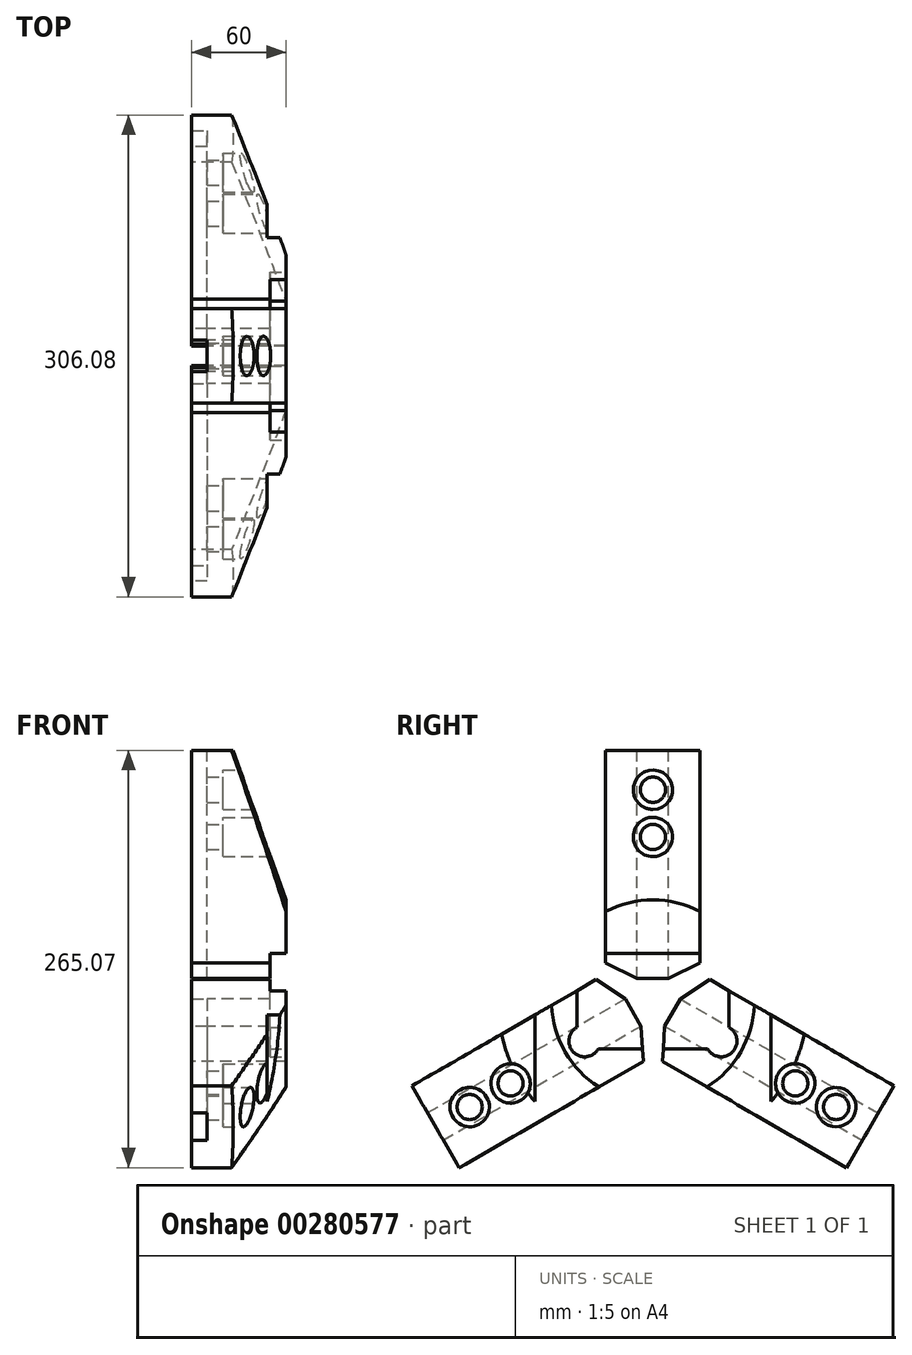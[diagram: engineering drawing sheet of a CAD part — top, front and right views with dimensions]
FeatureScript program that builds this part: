
annotation { "Feature Type Name" : "Feature", "Feature Type Description" : "" }
export const myFeature = defineFeature(function(context is Context, id is Id, definition is map)
    precondition{}
    {
        {
            var Q0;
            Q0=qCreatedBy(makeId("Right.planeOp"),FACE);
            var sketch = newSketch(context, id + "F0", { "sketchPlane" : qUnion([Q0])});
            skCircle(sketch, "E0", {"center": v(0, 0) * mm, "radius": 14.4 * mm});
            skLineSegment(sketch, "E1", {"start": v(0, 198.34) * mm, "end": v(0, 14.4) * mm, "construction": true});
            skLineSegment(sketch, "E2", {"start": v(0, 14.39) * mm, "end": v(0, -30.8) * mm, "construction": true});
            skLineSegment(sketch, "E3", {"start": v(0, 14.39) * mm, "end": v(10, 14.4) * mm});
            skLineSegment(sketch, "E4", {"start": v(10, 14.4) * mm, "end": v(30, 24.39) * mm});
            skLineSegment(sketch, "E5", {"start": v(30, 24.39) * mm, "end": v(30, 159.39) * mm});
            skLineSegment(sketch, "E6", {"start": v(30, 159.39) * mm, "end": v(0, 159.39) * mm});
            skLineSegment(sketch, "E7", {"start": v(0, 159.39) * mm, "end": v(-30, 159.39) * mm});
            skLineSegment(sketch, "E8", {"start": v(-30, 159.39) * mm, "end": v(-30, 24.39) * mm});
            skLineSegment(sketch, "E9", {"start": v(-30, 24.39) * mm, "end": v(-10, 14.39) * mm});
            skLineSegment(sketch, "E10", {"start": v(-10, 14.4) * mm, "end": v(0, 14.4) * mm});
            skSolve(sketch);
        }
        {
            var Q0;
            Q0=makeQuery(id+"F0.imprint","IMPRINT",FACE,{"disambiguationData":[TD([[makeQuery(id+"F0.imprint","IMPRINT",EDGE,{"derivedFrom":sQuery(id+"F0.wireOp",EDGE,"E3")}),1.0]])]});
            extrude(context, id + "F1", {"entities" : qUnion([Q0]), "depth" : 60 * mm});
        }
        {
            var Q0;
            Q0=makeQuery(id+"F1.opExtrude","CAP_FACE",FACE,{"disambiguationData":[OSD([sQuery(id+"F0.wireOp",EDGE,"E3"),sQuery(id+"F0.wireOp",EDGE,"E4"),sQuery(id+"F0.wireOp",EDGE,"E5"),sQuery(id+"F0.wireOp",EDGE,"E6"),sQuery(id+"F0.wireOp",EDGE,"E7"),sQuery(id+"F0.wireOp",EDGE,"E8"),sQuery(id+"F0.wireOp",EDGE,"E9"),sQuery(id+"F0.wireOp",EDGE,"E10")])],"isStart":false});
            var sketch = newSketch(context, id + "F2", { "sketchPlane" : qUnion([Q0])});
            skCircle(sketch, "E11", {"center": v(0, 134.39) * mm, "radius": 8 * mm});
            skCircle(sketch, "E12", {"center": v(0, 104.39) * mm, "radius": 8 * mm});
            skCircle(sketch, "E13", {"center": v(0, 134.39) * mm, "radius": 12.5 * mm});
            skCircle(sketch, "E14", {"center": v(0, 104.39) * mm, "radius": 12.5 * mm});
            skSolve(sketch);
        }
        {
            var Q0;
            Q0=makeQuery(id+"F2.imprint","IMPRINT",FACE,{"disambiguationData":[TD([[makeQuery(id+"F2.imprint","IMPRINT",EDGE,{"derivedFrom":sQuery(id+"F2.wireOp",EDGE,"E11")}),1.0]])]});
            var Q1;
            Q1=makeQuery(id+"F2.imprint","IMPRINT",FACE,{"disambiguationData":[TD([[makeQuery(id+"F2.imprint","IMPRINT",EDGE,{"derivedFrom":sQuery(id+"F2.wireOp",EDGE,"E12")}),1.0]])]});
            extrude(context, id + "F3", {"entities" : qUnion([Q0, Q1]), "operationType" : NewBodyOperationType.REMOVE, "endBound" : BoundingType.UP_TO_NEXT, "oppositeDirection" : true, "depth" : 25 * mm});
        }
        {
            var Q0;
            Q0=qSketchRegion(id+"F2",true);
            extrude(context, id + "F4", {"entities" : qUnion([Q0]), "operationType" : NewBodyOperationType.REMOVE, "oppositeDirection" : true, "depth" : 40 * mm});
        }
        {
            var Q0;
            Q0=makeQuery(id+"F1.opExtrude","SWEPT_FACE",FACE,{"disambiguationData":[OSD([sQuery(id+"F0.wireOp",EDGE,"E6"),sQuery(id+"F0.wireOp",EDGE,"E7")])]});
            var sketch = newSketch(context, id + "F5", { "sketchPlane" : qUnion([Q0])});
            skLineSegment(sketch, "E15", {"start": v(0, 0) * mm, "end": v(0, -10) * mm});
            skLineSegment(sketch, "E16", {"start": v(0, -10) * mm, "end": v(10, -10) * mm});
            skLineSegment(sketch, "E17", {"start": v(10, -10) * mm, "end": v(10, 0) * mm});
            skLineSegment(sketch, "E18", {"start": v(10, 0) * mm, "end": v(10, 10) * mm});
            skLineSegment(sketch, "E19", {"start": v(10, 10) * mm, "end": v(0, 10) * mm});
            skLineSegment(sketch, "E20", {"start": v(0, 10) * mm, "end": v(0, 0) * mm});
            skSolve(sketch);
        }
        {
            var Q0;
            Q0=qSketchRegion(id+"F5",true);
            var Q1;
            Q1=makeQuery(id+"F1.opExtrude","SWEPT_FACE",FACE,{"disambiguationData":[OSD([sQuery(id+"F0.wireOp",EDGE,"E3"),sQuery(id+"F0.wireOp",EDGE,"E10")])]});
            extrude(context, id + "F6", {"entities" : qUnion([Q0]), "operationType" : NewBodyOperationType.REMOVE, "endBound" : BoundingType.UP_TO_SURFACE, "oppositeDirection" : true, "endBoundEntityFace" : qUnion([Q1]), "depth" : 25 * mm});
        }
        {
            var Q0;
            Q0=qCreatedBy(makeId("Front.planeOp"),FACE);
            var sketch = newSketch(context, id + "F7", { "sketchPlane" : qUnion([Q0])});
            skLineSegment(sketch, "E21", {"start": v(0, 0) * mm, "end": v(73.98, 0) * mm, "construction": true});
            skSolve(sketch);
        }
        {
            var Q0;
            Q0=makeQuery(id+"F1.opExtrude","SWEPT_BODY",BODY,{"disambiguationData":[OSD([sQuery(id+"F0.wireOp",EDGE,"E3"),sQuery(id+"F0.wireOp",EDGE,"E4"),sQuery(id+"F0.wireOp",EDGE,"E5"),sQuery(id+"F0.wireOp",EDGE,"E6"),sQuery(id+"F0.wireOp",EDGE,"E7"),sQuery(id+"F0.wireOp",EDGE,"E8"),sQuery(id+"F0.wireOp",EDGE,"E9"),sQuery(id+"F0.wireOp",EDGE,"E10")])]});
            var Q1;
            Q1=sQuery(id+"F7.wireOp",EDGE,"E21");
            circularPattern(context, id + "F8", {"entities" : qUnion([Q0]), "axis" : qUnion([Q1]), "angle" : 360 * degree, "instanceCount" : 3, "equalSpace" : true, "computeTransformsWithoutBuiltin" : true});
        }
        {
            var Q0;
            Q0=makeQuery(id+"F1.opExtrude","SWEPT_BODY",BODY,{"disambiguationData":[OSD([sQuery(id+"F0.wireOp",EDGE,"E3"),sQuery(id+"F0.wireOp",EDGE,"E4"),sQuery(id+"F0.wireOp",EDGE,"E5"),sQuery(id+"F0.wireOp",EDGE,"E6"),sQuery(id+"F0.wireOp",EDGE,"E7"),sQuery(id+"F0.wireOp",EDGE,"E8"),sQuery(id+"F0.wireOp",EDGE,"E9"),sQuery(id+"F0.wireOp",EDGE,"E10")])]});
            var Q1;
            Q1=makeQuery(id+"F8.opPattern","COPY",BODY,{"derivedFrom":makeQuery(id+"F1.opExtrude","SWEPT_BODY",BODY,{"disambiguationData":[OSD([sQuery(id+"F0.wireOp",EDGE,"E3"),sQuery(id+"F0.wireOp",EDGE,"E4"),sQuery(id+"F0.wireOp",EDGE,"E5"),sQuery(id+"F0.wireOp",EDGE,"E6"),sQuery(id+"F0.wireOp",EDGE,"E7"),sQuery(id+"F0.wireOp",EDGE,"E8"),sQuery(id+"F0.wireOp",EDGE,"E9"),sQuery(id+"F0.wireOp",EDGE,"E10")])]}),"instanceName":"1"});
            var Q2;
            Q2=makeQuery(id+"F8.opPattern","COPY",BODY,{"derivedFrom":makeQuery(id+"F1.opExtrude","SWEPT_BODY",BODY,{"disambiguationData":[OSD([sQuery(id+"F0.wireOp",EDGE,"E3"),sQuery(id+"F0.wireOp",EDGE,"E4"),sQuery(id+"F0.wireOp",EDGE,"E5"),sQuery(id+"F0.wireOp",EDGE,"E6"),sQuery(id+"F0.wireOp",EDGE,"E7"),sQuery(id+"F0.wireOp",EDGE,"E8"),sQuery(id+"F0.wireOp",EDGE,"E9"),sQuery(id+"F0.wireOp",EDGE,"E10")])]}),"instanceName":"2"});
            transform(context, id + "F9", {"entities" : qUnion([Q0, Q1, Q2]), "transformType" : TransformType.TRANSLATION_3D, "dx" : 3 * mm, "dy" : 0 * mm, "dz" : 0 * mm, "makeCopy" : false});
        }
        {
            var Q0;
            Q0=makeQuery(id+"F1.opExtrude","CAP_FACE",FACE,{"disambiguationData":[OSD([sQuery(id+"F0.wireOp",EDGE,"E3"),sQuery(id+"F0.wireOp",EDGE,"E4"),sQuery(id+"F0.wireOp",EDGE,"E5"),sQuery(id+"F0.wireOp",EDGE,"E6"),sQuery(id+"F0.wireOp",EDGE,"E7"),sQuery(id+"F0.wireOp",EDGE,"E8"),sQuery(id+"F0.wireOp",EDGE,"E9"),sQuery(id+"F0.wireOp",EDGE,"E10")])],"isStart":false});
            var sketch = newSketch(context, id + "F10", { "sketchPlane" : qUnion([Q0])});
            skLineSegment(sketch, "E22.bottom", {"start": v(-34.71, -30.25) * mm, "end": v(34.71, -30.25) * mm});
            skLineSegment(sketch, "E22.top", {"start": v(-34.71, 30.25) * mm, "end": v(34.71, 30.25) * mm});
            skLineSegment(sketch, "E22.left", {"start": v(-48.38, -16.59) * mm, "end": v(-48.38, 16.59) * mm});
            skLineSegment(sketch, "E22.right", {"start": v(48.38, -16.59) * mm, "end": v(48.38, 16.59) * mm});
            skPoint(sketch, "E22.middle", {"position": v(0, 0) * mm});
            skPoint(sketch, "E23", {"position": v(-43.38, 25.25) * mm});
            skPoint(sketch, "E24", {"position": v(43.38, 25.25) * mm});
            skPoint(sketch, "E25", {"position": v(-43.38, -25.25) * mm});
            skPoint(sketch, "E26", {"position": v(43.38, -25.25) * mm});
            skArc(sketch, "E27", {"start": v(-34.71, 30.25) * mm, "mid": v(-50.45, 32.32) * mm, "end": v(-48.38, 16.59) * mm});
            skArc(sketch, "E28", {"start": v(48.37, 16.59) * mm, "mid": v(50.45, 32.32) * mm, "end": v(34.71, 30.25) * mm});
            skArc(sketch, "E29", {"start": v(34.71, -30.25) * mm, "mid": v(50.45, -32.32) * mm, "end": v(48.38, -16.59) * mm});
            skArc(sketch, "E30", {"start": v(-48.38, -16.59) * mm, "mid": v(-50.45, -32.32) * mm, "end": v(-34.71, -30.25) * mm});
            skSolve(sketch);
        }
        {
            var Q0;
            Q0=makeQuery(id+"F10.imprint","IMPRINT",FACE,{"disambiguationData":[TD([[makeQuery(id+"F10.imprint","IMPRINT",EDGE,{"derivedFrom":sQuery(id+"F10.wireOp",EDGE,"E22.bottom")}),1.0]])]});
            var Q1;
            {var subQ5=makeQuery(id+"F1.opExtrude","CAP_EDGE",EDGE,{"disambiguationData":[OSD([sQuery(id+"F0.wireOp",EDGE,"E3"),sQuery(id+"F0.wireOp",EDGE,"E10")])],"isStart":false});Q1=makeQuery(id+"F10.imprint","IMPRINT",FACE,{"disambiguationData":[TD([[makeQuery(id+"F10.imprint","IMPRINT",EDGE,{"derivedFrom":subQ5}),1.0]])]});}
            extrude(context, id + "F11", {"entities" : qUnion([Q0, Q1]), "operationType" : NewBodyOperationType.REMOVE, "oppositeDirection" : true, "depth" : 10.3 * mm, "offsetDistance" : 25 * mm});
        }
        {
            var Q0;
            Q0=qCreatedBy(makeId("Front.planeOp"),FACE);
            var sketch = newSketch(context, id + "F12", { "sketchPlane" : qUnion([Q0])});
            skLineSegment(sketch, "E31", {"start": v(0, 0) * mm, "end": v(61.97, 0) * mm, "construction": true});
            skLineSegment(sketch, "E32", {"start": v(29.5, 159.39) * mm, "end": v(63, 64.39) * mm});
            skLineSegment(sketch, "E33", {"start": v(63, 64.39) * mm, "end": v(63, 159.39) * mm});
            skLineSegment(sketch, "E34", {"start": v(63, 159.39) * mm, "end": v(29.5, 159.39) * mm});
            skLineSegment(sketch, "E35", {"start": v(29.5, 159.39) * mm, "end": v(28.09, 163.39) * mm});
            skLineSegment(sketch, "E36", {"start": v(28.09, 163.39) * mm, "end": v(63, 163.39) * mm});
            skLineSegment(sketch, "E37", {"start": v(63, 163.39) * mm, "end": v(63, 159.39) * mm});
            skSolve(sketch);
        }
        {
            var Q0;
            Q0 = qSketchRegion(id + "F12", true);
            var Q1;
            Q1=sQuery(id+"F12.wireOp",EDGE,"E31");
            revolve(context, id + "F13", {"operationType" : NewBodyOperationType.REMOVE, "surfaceOperationType" : NewSurfaceOperationType.NEW, "entities" : qUnion([Q0]), "axis" : qUnion([Q1]), "revolveType" : RevolveType.FULL, "oppositeDirection" : true});
        }
        {
            var Q0;
            Q0=qCreatedBy(makeId("Top.planeOp"),FACE);
            var sketch = newSketch(context, id + "F14", { "sketchPlane" : qUnion([Q0])});
            skLineSegment(sketch, "E38.bottom", {"start": v(86, 75) * mm, "end": v(51, 75) * mm});
            skLineSegment(sketch, "E38.top", {"start": v(86, 135) * mm, "end": v(51, 135) * mm});
            skLineSegment(sketch, "E38.left", {"start": v(86, 75) * mm, "end": v(86, 135) * mm});
            skLineSegment(sketch, "E38.right", {"start": v(51, 75) * mm, "end": v(51, 135) * mm});
            skLineSegment(sketch, "E39", {"start": v(0, 0) * mm, "end": v(77.23, 0) * mm, "construction": true});
            skLineSegment(sketch, "E40.MirrorCS", {"start": v(86, -75) * mm, "end": v(86, -135) * mm});
            skLineSegment(sketch, "E41.MirrorCS", {"start": v(86, -135) * mm, "end": v(51, -135) * mm});
            skLineSegment(sketch, "E42.MirrorCS", {"start": v(51, -75) * mm, "end": v(51, -135) * mm});
            skLineSegment(sketch, "E43.MirrorCS", {"start": v(86, -75) * mm, "end": v(51, -75) * mm});
            skSolve(sketch);
        }
        {
            var Q0;
            Q0 = qSketchRegion(id + "F14", true);
            extrude(context, id + "F15", {"entities" : qUnion([Q0]), "operationType" : NewBodyOperationType.REMOVE, "endBound" : BoundingType.THROUGH_ALL, "oppositeDirection" : true, "depth" : 25 * mm, "offsetDistance" : 25 * mm});
        }
    });
